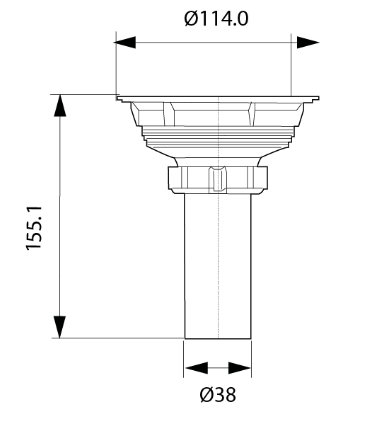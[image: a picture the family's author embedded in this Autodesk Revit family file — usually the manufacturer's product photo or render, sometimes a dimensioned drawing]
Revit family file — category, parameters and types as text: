
# Revit family: 135216851_Mueble Pontus Vital 45 cm con Lavamanos
name_source: partatom
category: Furniture
units: mm (PartAtom-declared; Revit-internal decimal feet)

## family parameters
Always vertical = Yes
Cut with Voids When Loaded = No
OmniClass Number = 23.31.13.11
OmniClass Title = Single Sinks
Room Calculation Point = No
Shared = No
Work Plane-Based = No

## types (1)
- 135216851_Mueble Pontus Vital 45 cm con Lavamanos
    Acabado = Corona_Plastico_Taupe
    Alto = 764 mm  [stored 2.50656 ft]
    Ancho = 450 mm  [stored 1.47638 ft]
    Creado por = IDD
    Description = Línea de Muebles Pontus Vital diseño compacto que se adapta a la gran mayoría de
espacios disponibles.
· Diseño de apertura cómodo.
· Máxima capacidad de almacenamiento.
· Lavamanos 100% en porcelana con superficie amplia de apoyo.
· Resistentes a la humedad.
    Fecha de creación = 30/07/2020
    Garantía = 5 Años  (Madera)
    Garantía Herraje = 1 Años
    Longitud = 450 mm  [stored 1.47638 ft]
    Manufacturer = Corona
    Material = Corona_Madera_Coñac
    Model = Pontus Vital 45
    Peso Bruto aprox = 22,5 lb (10,2 kg).
    Peso Neto aprox = 21,2 lb (9,6 kg).
    Resistencia a la humedad = 8%.
    Resistencia al rayado = 700 ciclos
    URL = https://corona.co

note: [stored X ft] marks values corroborated as IEEE doubles in the binary element streams (Revit-internal decimal feet)

## geometry (parser evidence)
native form markers: Sweep x11
no freeform markers — native parametric forms only
